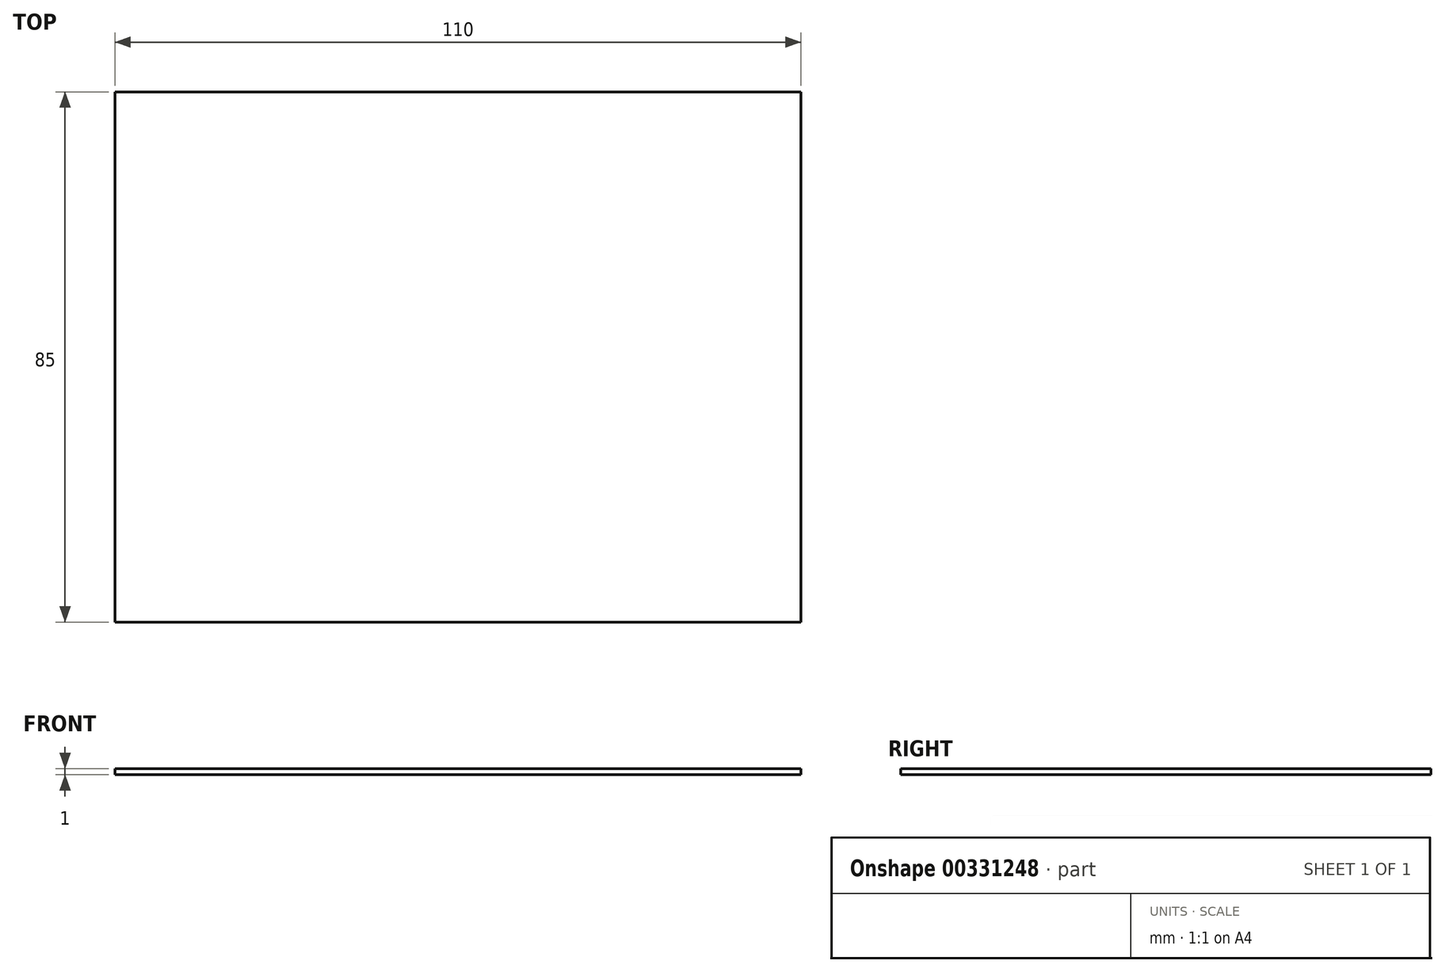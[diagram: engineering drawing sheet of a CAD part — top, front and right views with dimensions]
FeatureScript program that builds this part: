
annotation { "Feature Type Name" : "Feature", "Feature Type Description" : "" }
export const myFeature = defineFeature(function(context is Context, id is Id, definition is map)
    precondition{}
    {
        {
            var Q0;
            Q0=qCreatedBy(makeId("Top.planeOp"),FACE);
            var sketch = newSketch(context, id + "F0", { "sketchPlane" : qUnion([Q0])});
            skLineSegment(sketch, "E0.bottom", {"start": v(-55, 42.5) * mm, "end": v(55, 42.5) * mm});
            skLineSegment(sketch, "E0.top", {"start": v(-55, -42.5) * mm, "end": v(55, -42.5) * mm});
            skLineSegment(sketch, "E0.left", {"start": v(-55, 42.5) * mm, "end": v(-55, -42.5) * mm});
            skLineSegment(sketch, "E0.right", {"start": v(55, 42.5) * mm, "end": v(55, -42.5) * mm});
            skPoint(sketch, "E0.middle", {"position": v(0, 0) * mm});
            skSolve(sketch);
        }
        {
            var Q0;
            Q0 = qSketchRegion(id + "F0", true);
            extrude(context, id + "F1", {"entities" : qUnion([Q0]), "depth" : 1 * mm});
        }
        {
            var Q0;
            Q0=qCreatedBy(makeId("Front.planeOp"),FACE);
            cPlane(context, id + "F2", {"entities" : qUnion([Q0]), "cplaneType" : CPlaneType.OFFSET, "offset" : 42.5 * mm, "oppositeDirection" : true, "width" : 150 * mm, "height" : 150 * mm});
        }
    });
